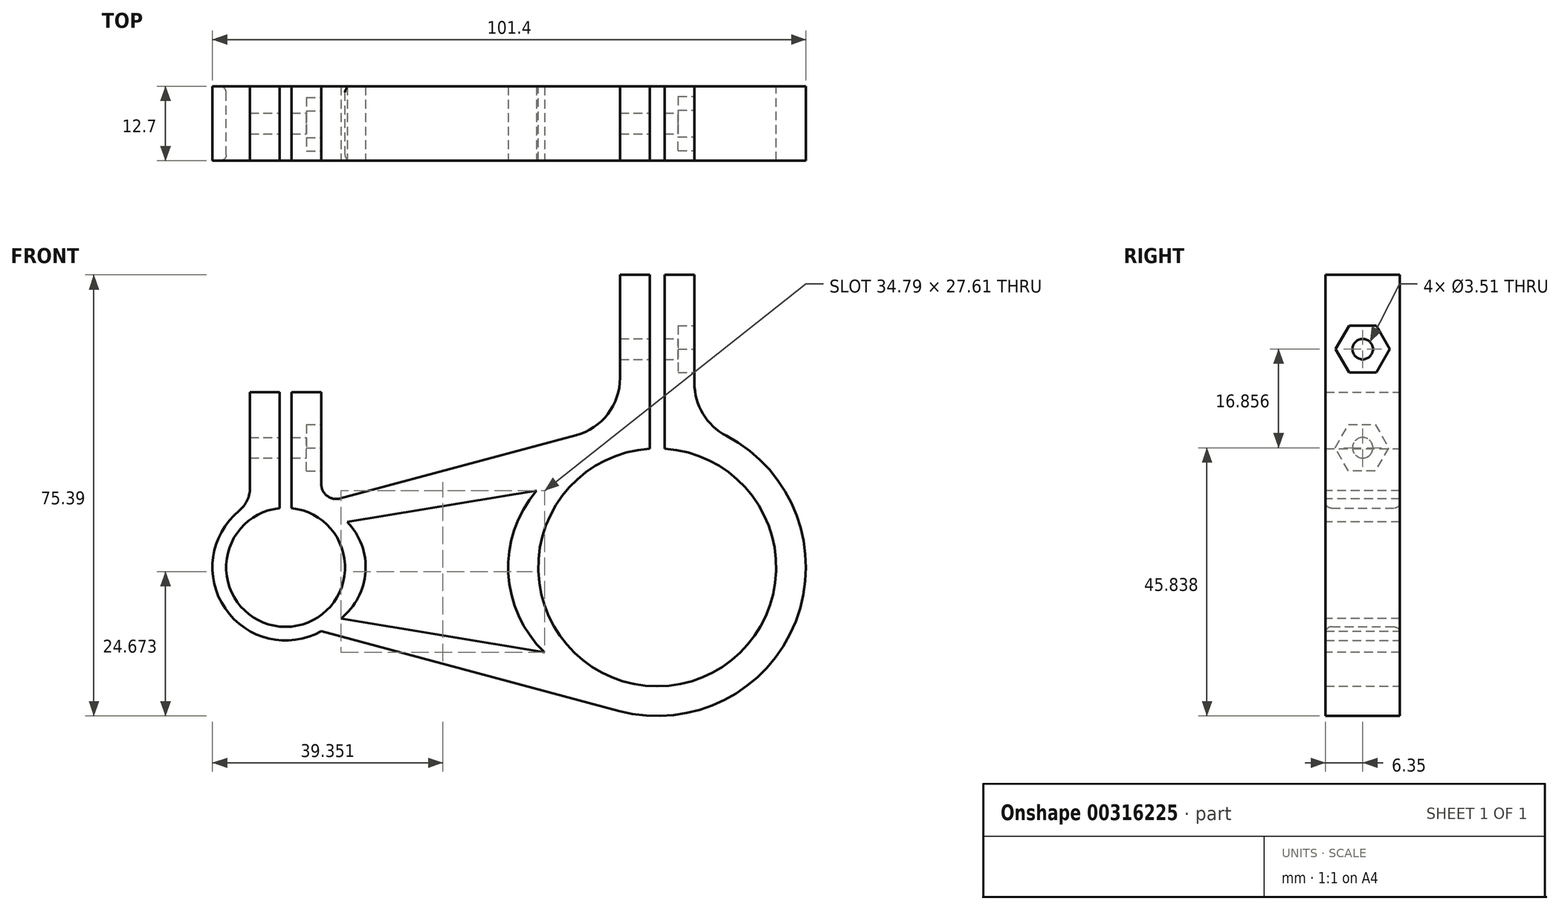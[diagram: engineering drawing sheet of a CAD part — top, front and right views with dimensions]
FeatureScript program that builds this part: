
annotation { "Feature Type Name" : "Feature", "Feature Type Description" : "" }
export const myFeature = defineFeature(function(context is Context, id is Id, definition is map)
    precondition{}
    {
        {
            var Q0;
            Q0=qCreatedBy(makeId("Front.planeOp"),FACE);
            var sketch = newSketch(context, id + "F0", { "sketchPlane" : qUnion([Q0])});
            skArc(sketch, "E0", {"start": v(-6.35, 24.6) * mm, "mid": v(-6.57, 24.53) * mm, "end": v(-6.8, 24.47) * mm});
            skArc(sketch, "E1", {"start": v(-1.27, 20.28) * mm, "mid": v(0, -20.32) * mm, "end": v(1.27, 20.28) * mm});
            skLineSegment(sketch, "E2", {"start": v(-1.27, 25.37) * mm, "end": v(-1.27, 20.28) * mm});
            skLineSegment(sketch, "E3.MirrorCS", {"start": v(1.27, 25.37) * mm, "end": v(1.27, 20.28) * mm});
            skLineSegment(sketch, "E4", {"start": v(-1.27, 25.37) * mm, "end": v(-1.27, 50) * mm});
            skLineSegment(sketch, "E5", {"start": v(-1.27, 50) * mm, "end": v(-6.35, 50) * mm});
            skLineSegment(sketch, "E6", {"start": v(-6.35, 50) * mm, "end": v(-6.35, 24.6) * mm});
            skLineSegment(sketch, "E7.MirrorCS", {"start": v(1.27, 25.37) * mm, "end": v(1.27, 50) * mm});
            skLineSegment(sketch, "E8.MirrorCS", {"start": v(6.35, 50) * mm, "end": v(6.35, 24.6) * mm});
            skLineSegment(sketch, "E9.MirrorCS", {"start": v(1.27, 50) * mm, "end": v(6.35, 50) * mm});
            skArc(sketch, "E10", {"start": v(-64.52, 10.1) * mm, "mid": v(-63.5, -10.16) * mm, "end": v(-62.48, 10.1) * mm});
            skArc(sketch, "E11", {"start": v(-69.6, 10.91) * mm, "mid": v(-74.41, -6.1) * mm, "end": v(-57.4, -10.91) * mm});
            skLineSegment(sketch, "E12", {"start": v(-63.5, 0) * mm, "end": v(-63.5, 44.67) * mm, "construction": true});
            skLineSegment(sketch, "E13", {"start": v(-64.52, 12.46) * mm, "end": v(-64.52, 10.1) * mm});
            skLineSegment(sketch, "E14.MirrorCS", {"start": v(-62.48, 12.46) * mm, "end": v(-62.48, 10.1) * mm});
            skLineSegment(sketch, "E15", {"start": v(-64.52, 12.46) * mm, "end": v(-64.52, 29.96) * mm});
            skLineSegment(sketch, "E16", {"start": v(-64.52, 29.96) * mm, "end": v(-69.6, 29.96) * mm});
            skLineSegment(sketch, "E17", {"start": v(-69.6, 29.96) * mm, "end": v(-69.6, 10.91) * mm});
            skLineSegment(sketch, "E18.MirrorCS", {"start": v(-62.48, 12.46) * mm, "end": v(-62.48, 29.96) * mm});
            skLineSegment(sketch, "E19.MirrorCS", {"start": v(-57.4, 29.96) * mm, "end": v(-57.4, 10.91) * mm});
            skLineSegment(sketch, "E20.MirrorCS", {"start": v(-62.48, 29.96) * mm, "end": v(-57.4, 29.96) * mm});
            skLineSegment(sketch, "E21", {"start": v(0, 0) * mm, "end": v(-63.5, 0) * mm, "construction": true});
            skLineSegment(sketch, "E22", {"start": v(-57.4, 10.91) * mm, "end": v(-6.35, 24.6) * mm});
            skLineSegment(sketch, "E23", {"start": v(-57.4, -10.91) * mm, "end": v(-6.35, -24.6) * mm});
            skArc(sketch, "E24.trimOffspring", {"start": v(-6.57, -24.53) * mm, "mid": v(24.56, -6.46) * mm, "end": v(6.35, 24.6) * mm});
            skSolve(sketch);
        }
        {
            var Q0;
            Q0=makeQuery(id+"F0.imprint","IMPRINT",FACE,{"disambiguationData":[TD([[makeQuery(id+"F0.imprint","IMPRINT",EDGE,{"derivedFrom":sQuery(id+"F0.wireOp",EDGE,"E1")}),-1.0]])]});
            extrude(context, id + "F1", {"entities" : qUnion([Q0]), "depth" : 12.7 * mm});
        }
        {
            var Q0;
            Q0=makeQuery(id+"F1.opExtrude","SWEPT_FACE",FACE,{"disambiguationData":[OSD([sQuery(id+"F0.wireOp",EDGE,"E8.MirrorCS")])]});
            var sketch = newSketch(context, id + "F2", { "sketchPlane" : qUnion([Q0])});
            skCircle(sketch, "E25.cCircle", {"center": v(-6.35, 37.3) * mm, "radius": 4 * mm, "construction": true});
            skLineSegment(sketch, "E25.0", {"start": v(-4.04, 33.3) * mm, "end": v(-8.66, 33.3) * mm});
            skLineSegment(sketch, "E25.1", {"start": v(-8.66, 33.3) * mm, "end": v(-10.97, 37.3) * mm});
            skLineSegment(sketch, "E25.2", {"start": v(-10.97, 37.3) * mm, "end": v(-8.66, 41.3) * mm});
            skLineSegment(sketch, "E25.3", {"start": v(-8.66, 41.3) * mm, "end": v(-4.04, 41.3) * mm});
            skLineSegment(sketch, "E25.4", {"start": v(-4.04, 41.3) * mm, "end": v(-1.73, 37.3) * mm});
            skLineSegment(sketch, "E25.5", {"start": v(-1.73, 37.3) * mm, "end": v(-4.04, 33.3) * mm});
            skPoint(sketch, "E25.0.midPoint", {"position": v(-6.35, 33.3) * mm});
            skPoint(sketch, "E26", {"position": v(-10.97, 37.3) * mm});
            skPoint(sketch, "E27", {"position": v(-1.73, 37.3) * mm});
            skSolve(sketch);
        }
        {
            var Q0;
            Q0=makeQuery(id+"F2.imprint","IMPRINT",FACE,{"disambiguationData":[TD([[makeQuery(id+"F2.imprint","IMPRINT",EDGE,{"derivedFrom":sQuery(id+"F2.wireOp",EDGE,"E25.0")}),-1.0]])]});
            extrude(context, id + "F3", {"entities" : qUnion([Q0]), "operationType" : NewBodyOperationType.REMOVE, "oppositeDirection" : true, "depth" : 2.78 * mm});
        }
        {
            var Q0;
            Q0=makeQuery(id+"F3.boolean.opBoolean","COPY",FACE,{"derivedFrom":makeQuery(id+"F3.opExtrude","CAP_FACE",FACE,{"disambiguationData":[OSD([sQuery(id+"F2.wireOp",EDGE,"E25.0"),sQuery(id+"F2.wireOp",EDGE,"E25.1"),sQuery(id+"F2.wireOp",EDGE,"E25.2"),sQuery(id+"F2.wireOp",EDGE,"E25.3"),sQuery(id+"F2.wireOp",EDGE,"E25.4"),sQuery(id+"F2.wireOp",EDGE,"E25.5")])],"isStart":false})});
            var sketch = newSketch(context, id + "F4", { "sketchPlane" : qUnion([Q0])});
            skPoint(sketch, "E28", {"position": v(-6.35, 37.3) * mm});
            skSolve(sketch);
        }
        {
            var Q0;
            Q0=sQuery(id+"F4.wireOp",VERTEX,"E28");
            var Q1;
            Q1=makeQuery(id+"F1.opExtrude","SWEPT_BODY",BODY,{"disambiguationData":[OSD([sQuery(id+"F0.wireOp",EDGE,"E1"),sQuery(id+"F0.wireOp",EDGE,"E2"),sQuery(id+"F0.wireOp",EDGE,"E3.MirrorCS"),sQuery(id+"F0.wireOp",EDGE,"E4"),sQuery(id+"F0.wireOp",EDGE,"E5"),sQuery(id+"F0.wireOp",EDGE,"E6"),sQuery(id+"F0.wireOp",EDGE,"E7.MirrorCS"),sQuery(id+"F0.wireOp",EDGE,"E8.MirrorCS"),sQuery(id+"F0.wireOp",EDGE,"E9.MirrorCS"),sQuery(id+"F0.wireOp",EDGE,"E10"),sQuery(id+"F0.wireOp",EDGE,"E11"),sQuery(id+"F0.wireOp",EDGE,"E13"),sQuery(id+"F0.wireOp",EDGE,"E14.MirrorCS"),sQuery(id+"F0.wireOp",EDGE,"E15"),sQuery(id+"F0.wireOp",EDGE,"E16"),sQuery(id+"F0.wireOp",EDGE,"E17"),sQuery(id+"F0.wireOp",EDGE,"E18.MirrorCS"),sQuery(id+"F0.wireOp",EDGE,"E19.MirrorCS"),sQuery(id+"F0.wireOp",EDGE,"E20.MirrorCS"),sQuery(id+"F0.wireOp",EDGE,"E22"),sQuery(id+"F0.wireOp",EDGE,"E23"),sQuery(id+"F0.wireOp",EDGE,"E24.trimOffspring")])]});
            hole(context, id + "F5", {"style" : HoleStyle.SIMPLE, "endStyle" : HoleEndStyle.BLIND, "holeDiameter" : 3.5 * mm, "holeDepth" : 19.05 * mm, "tappedDepth" : 12.7 * mm, "tapClearance" : 3, "locations" : qUnion([Q0]), "scope" : qUnion([Q1])});
        }
        {
            var Q0;
            Q0=makeQuery(id+"F1.opExtrude","SWEPT_FACE",FACE,{"disambiguationData":[OSD([sQuery(id+"F0.wireOp",EDGE,"E19.MirrorCS")])]});
            var sketch = newSketch(context, id + "F6", { "sketchPlane" : qUnion([Q0])});
            skCircle(sketch, "E29.cCircle", {"center": v(-6.48, 20.44) * mm, "radius": 3.97 * mm, "construction": true});
            skLineSegment(sketch, "E29.0", {"start": v(-8.78, 16.47) * mm, "end": v(-11.07, 20.44) * mm});
            skLineSegment(sketch, "E29.1", {"start": v(-11.07, 20.44) * mm, "end": v(-8.78, 24.4) * mm});
            skLineSegment(sketch, "E29.2", {"start": v(-8.78, 24.4) * mm, "end": v(-4.2, 24.4) * mm});
            skLineSegment(sketch, "E29.3", {"start": v(-4.2, 24.4) * mm, "end": v(-1.9, 20.44) * mm});
            skLineSegment(sketch, "E29.4", {"start": v(-1.9, 20.44) * mm, "end": v(-4.2, 16.47) * mm});
            skLineSegment(sketch, "E29.5", {"start": v(-4.2, 16.47) * mm, "end": v(-8.78, 16.47) * mm});
            skPoint(sketch, "E29.0.midPoint", {"position": v(-9.92, 18.45) * mm});
            skSolve(sketch);
        }
        {
            var Q0;
            Q0=makeQuery(id+"F6.imprint","IMPRINT",FACE,{"disambiguationData":[TD([[makeQuery(id+"F6.imprint","IMPRINT",EDGE,{"derivedFrom":sQuery(id+"F6.wireOp",EDGE,"E29.0")}),-1.0]])]});
            extrude(context, id + "F7", {"entities" : qUnion([Q0]), "operationType" : NewBodyOperationType.REMOVE, "oppositeDirection" : true, "depth" : 2.54 * mm});
        }
        {
            var Q0;
            Q0=makeQuery(id+"F1.opExtrude","SWEPT_EDGE",EDGE,{"disambiguationData":[OSD([sQuery(id+"F0.wireOp",EDGE,"E0"),sQuery(id+"F0.wireOp",EDGE,"E6"),sQuery(id+"F0.wireOp",EDGE,"E22")])]});
            fillet(context, id + "F8", {"entities" : qUnion([Q0]), "radius" : 10.16 * mm, "tangentPropagation" : true, "allowEdgeOverflow" : false});
        }
        {
            var Q0;
            Q0=makeQuery(id+"F1.opExtrude","SWEPT_EDGE",EDGE,{"disambiguationData":[OSD([sQuery(id+"F0.wireOp",EDGE,"E8.MirrorCS"),sQuery(id+"F0.wireOp",EDGE,"E24.trimOffspring")])]});
            fillet(context, id + "F9", {"entities" : qUnion([Q0]), "radius" : 10.16 * mm, "tangentPropagation" : true, "allowEdgeOverflow" : false});
        }
        {
            var Q0;
            Q0=makeQuery(id+"F1.opExtrude","SWEPT_EDGE",EDGE,{"disambiguationData":[OSD([sQuery(id+"F0.wireOp",EDGE,"E19.MirrorCS"),sQuery(id+"F0.wireOp",EDGE,"E22")])]});
            fillet(context, id + "F10", {"entities" : qUnion([Q0]), "radius" : 2.54 * mm, "tangentPropagation" : true, "allowEdgeOverflow" : false});
        }
        {
            var Q0;
            Q0=makeQuery(id+"F1.opExtrude","SWEPT_EDGE",EDGE,{"disambiguationData":[OSD([sQuery(id+"F0.wireOp",EDGE,"E11"),sQuery(id+"F0.wireOp",EDGE,"E17")])]});
            fillet(context, id + "F11", {"entities" : qUnion([Q0]), "radius" : 5.08 * mm, "tangentPropagation" : true, "allowEdgeOverflow" : false});
        }
        {
            var Q0;
            Q0=makeQuery(id+"F1.opExtrude","CAP_FACE",FACE,{"disambiguationData":[OSD([sQuery(id+"F0.wireOp",EDGE,"E1"),sQuery(id+"F0.wireOp",EDGE,"E2"),sQuery(id+"F0.wireOp",EDGE,"E3.MirrorCS"),sQuery(id+"F0.wireOp",EDGE,"E4"),sQuery(id+"F0.wireOp",EDGE,"E5"),sQuery(id+"F0.wireOp",EDGE,"E6"),sQuery(id+"F0.wireOp",EDGE,"E7.MirrorCS"),sQuery(id+"F0.wireOp",EDGE,"E8.MirrorCS"),sQuery(id+"F0.wireOp",EDGE,"E9.MirrorCS"),sQuery(id+"F0.wireOp",EDGE,"E10"),sQuery(id+"F0.wireOp",EDGE,"E11"),sQuery(id+"F0.wireOp",EDGE,"E13"),sQuery(id+"F0.wireOp",EDGE,"E14.MirrorCS"),sQuery(id+"F0.wireOp",EDGE,"E15"),sQuery(id+"F0.wireOp",EDGE,"E16"),sQuery(id+"F0.wireOp",EDGE,"E17"),sQuery(id+"F0.wireOp",EDGE,"E18.MirrorCS"),sQuery(id+"F0.wireOp",EDGE,"E19.MirrorCS"),sQuery(id+"F0.wireOp",EDGE,"E20.MirrorCS"),sQuery(id+"F0.wireOp",EDGE,"E22"),sQuery(id+"F0.wireOp",EDGE,"E23"),sQuery(id+"F0.wireOp",EDGE,"E24.trimOffspring")])],"isStart":false});
            var sketch = newSketch(context, id + "F12", { "sketchPlane" : qUnion([Q0])});
            skArc(sketch, "E30", {"start": v(-54.04, -8.72) * mm, "mid": v(-49.85, -0.72) * mm, "end": v(-52.97, 7.76) * mm});
            skArc(sketch, "E31", {"start": v(-20.63, 13.08) * mm, "mid": v(-25.44, -1) * mm, "end": v(-19.26, -14.53) * mm});
            skLineSegment(sketch, "E32", {"start": v(-52.97, 7.76) * mm, "end": v(-20.63, 13.08) * mm});
            skLineSegment(sketch, "E33", {"start": v(-54.04, -8.72) * mm, "end": v(-19.26, -14.53) * mm});
            skSolve(sketch);
        }
        {
            var Q0;
            Q0=makeQuery(id+"F1.opExtrude","CAP_EDGE",EDGE,{"disambiguationData":[OSD([sQuery(id+"F0.wireOp",EDGE,"E10")])],"isStart":false});
            fillet(context, id + "F13", {"entities" : qUnion([Q0]), "radius" : 1 * mm, "tangentPropagation" : true, "allowEdgeOverflow" : false});
        }
        {
            var Q0;
            Q0=makeQuery(id+"F1.opExtrude","CAP_EDGE",EDGE,{"disambiguationData":[OSD([sQuery(id+"F0.wireOp",EDGE,"E10")])],"isStart":true});
            fillet(context, id + "F14", {"entities" : qUnion([Q0]), "radius" : 1 * mm, "tangentPropagation" : true, "allowEdgeOverflow" : false});
        }
        {
            var Q0;
            Q0=makeQuery(id+"F7.boolean.opBoolean","COPY",FACE,{"derivedFrom":makeQuery(id+"F7.opExtrude","CAP_FACE",FACE,{"disambiguationData":[OSD([sQuery(id+"F6.wireOp",EDGE,"E29.0"),sQuery(id+"F6.wireOp",EDGE,"E29.1"),sQuery(id+"F6.wireOp",EDGE,"E29.2"),sQuery(id+"F6.wireOp",EDGE,"E29.3"),sQuery(id+"F6.wireOp",EDGE,"E29.4"),sQuery(id+"F6.wireOp",EDGE,"E29.5")])],"isStart":false})});
            var sketch = newSketch(context, id + "F15", { "sketchPlane" : qUnion([Q0])});
            skPoint(sketch, "E34", {"position": v(-6.35, 20.44) * mm});
            skSolve(sketch);
        }
        {
            var Q0;
            Q0=sQuery(id+"F15.wireOp",VERTEX,"E34");
            var Q1;
            Q1=makeQuery(id+"F1.opExtrude","SWEPT_BODY",BODY,{"disambiguationData":[OSD([sQuery(id+"F0.wireOp",EDGE,"E1"),sQuery(id+"F0.wireOp",EDGE,"E2"),sQuery(id+"F0.wireOp",EDGE,"E3.MirrorCS"),sQuery(id+"F0.wireOp",EDGE,"E4"),sQuery(id+"F0.wireOp",EDGE,"E5"),sQuery(id+"F0.wireOp",EDGE,"E6"),sQuery(id+"F0.wireOp",EDGE,"E7.MirrorCS"),sQuery(id+"F0.wireOp",EDGE,"E8.MirrorCS"),sQuery(id+"F0.wireOp",EDGE,"E9.MirrorCS"),sQuery(id+"F0.wireOp",EDGE,"E10"),sQuery(id+"F0.wireOp",EDGE,"E11"),sQuery(id+"F0.wireOp",EDGE,"E13"),sQuery(id+"F0.wireOp",EDGE,"E14.MirrorCS"),sQuery(id+"F0.wireOp",EDGE,"E15"),sQuery(id+"F0.wireOp",EDGE,"E16"),sQuery(id+"F0.wireOp",EDGE,"E17"),sQuery(id+"F0.wireOp",EDGE,"E18.MirrorCS"),sQuery(id+"F0.wireOp",EDGE,"E19.MirrorCS"),sQuery(id+"F0.wireOp",EDGE,"E20.MirrorCS"),sQuery(id+"F0.wireOp",EDGE,"E22"),sQuery(id+"F0.wireOp",EDGE,"E23"),sQuery(id+"F0.wireOp",EDGE,"E24.trimOffspring")])]});
            hole(context, id + "F16", {"style" : HoleStyle.SIMPLE, "endStyle" : HoleEndStyle.BLIND, "holeDiameter" : 3.5 * mm, "holeDepth" : 12.7 * mm, "tappedDepth" : 12.7 * mm, "tapClearance" : 3, "locations" : qUnion([Q0]), "scope" : qUnion([Q1])});
        }
        {
            var Q0;
            Q0=makeQuery(id+"F12.imprint","IMPRINT",FACE,{"disambiguationData":[TD([[makeQuery(id+"F12.imprint","IMPRINT",EDGE,{"derivedFrom":sQuery(id+"F12.wireOp",EDGE,"E30")}),-1.0]])]});
            extrude(context, id + "F17", {"entities" : qUnion([Q0]), "operationType" : NewBodyOperationType.REMOVE, "oppositeDirection" : true, "depth" : 25 * mm});
        }
    });
